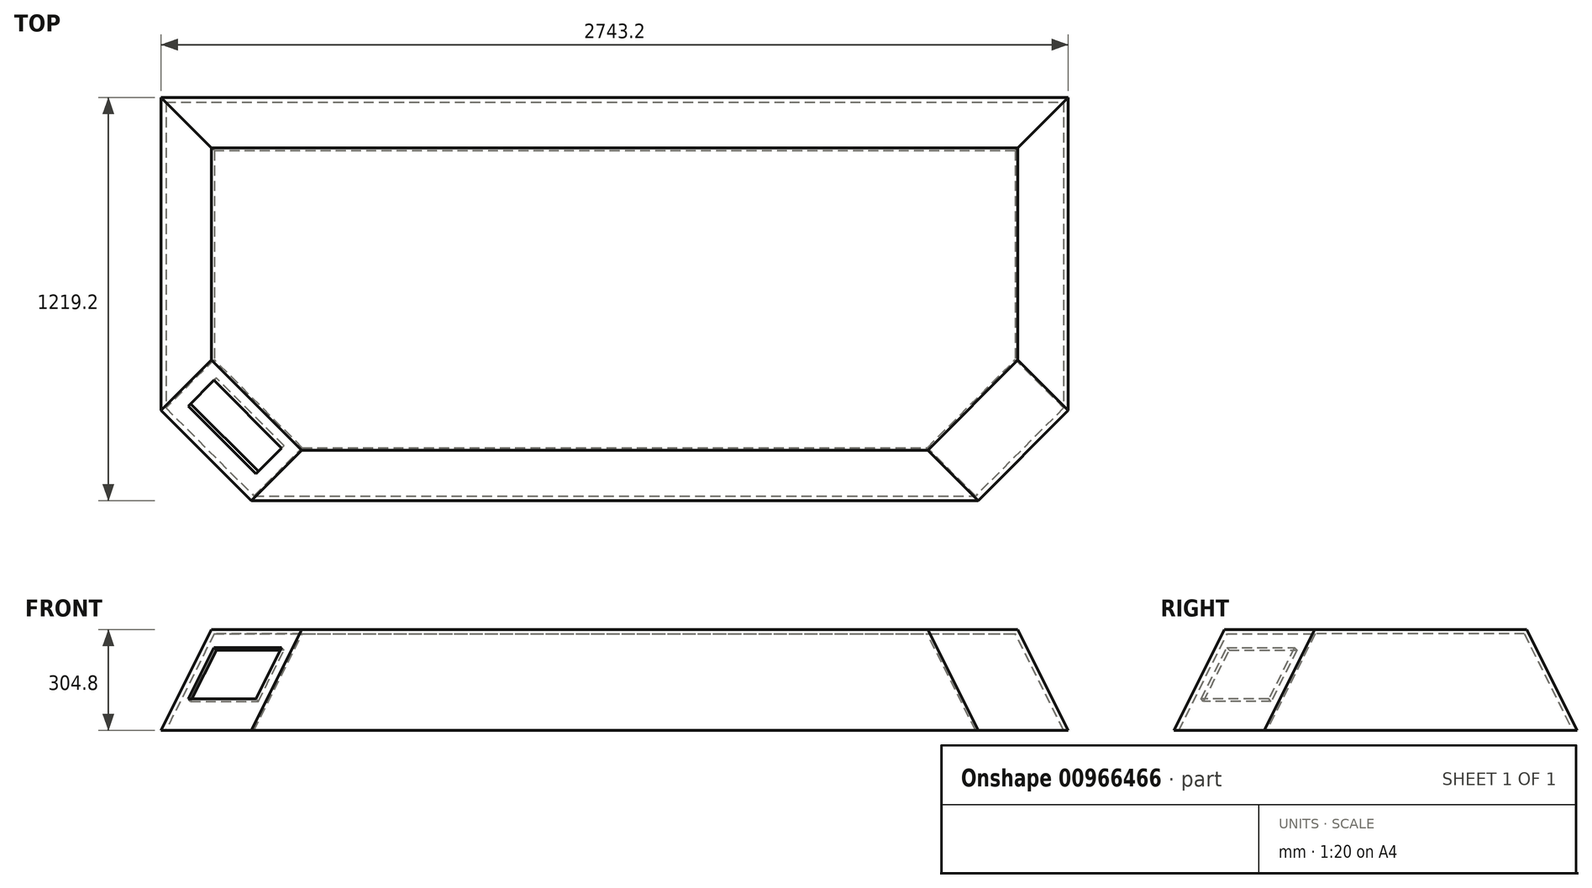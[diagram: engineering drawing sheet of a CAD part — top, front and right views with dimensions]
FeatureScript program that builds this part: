
annotation { "Feature Type Name" : "Feature", "Feature Type Description" : "" }
export const myFeature = defineFeature(function(context is Context, id is Id, definition is map)
    precondition{}
    {
        {
            var Q0;
            Q0=qCreatedBy(makeId("Top.planeOp"),FACE);
            var sketch = newSketch(context, id + "F0", { "sketchPlane" : qUnion([Q0])});
            skLineSegment(sketch, "E0.bottom", {"start": v(-1371.6, 609.6) * mm, "end": v(1371.6, 609.6) * mm});
            skLineSegment(sketch, "E0.top", {"start": v(-1371.6, -609.6) * mm, "end": v(1371.6, -609.6) * mm});
            skLineSegment(sketch, "E0.left", {"start": v(-1371.6, 609.6) * mm, "end": v(-1371.6, -609.6) * mm});
            skLineSegment(sketch, "E0.right", {"start": v(1371.6, 609.6) * mm, "end": v(1371.6, -609.6) * mm});
            skLineSegment(sketch, "E1", {"start": v(-1371.6, 609.6) * mm, "end": v(1371.6, -609.6) * mm, "construction": true});
            skLineSegment(sketch, "E2", {"start": v(-1371.6, -609.6) * mm, "end": v(1371.6, 609.6) * mm, "construction": true});
            skPoint(sketch, "E3", {"position": v(0, 0) * mm});
            skSolve(sketch);
        }
        {
            var Q0;
            Q0=qCreatedBy(makeId("Top.planeOp"),FACE);
            cPlane(context, id + "F1", {"entities" : qUnion([Q0]), "cplaneType" : CPlaneType.OFFSET, "offset" : 304.8 * mm, "width" : 152.4 * mm, "height" : 152.4 * mm});
        }
        {
            var Q0;
            Q0=qCreatedBy(id+"F1.planeOp",FACE);
            var sketch = newSketch(context, id + "F2", { "sketchPlane" : qUnion([Q0])});
            skLineSegment(sketch, "E4.0", {"start": v(-1219.2, 457.2) * mm, "end": v(1219.2, 457.2) * mm});
            skLineSegment(sketch, "E4.1", {"start": v(-1219.2, 457.2) * mm, "end": v(-1219.2, -457.2) * mm});
            skLineSegment(sketch, "E4.2", {"start": v(-1219.2, -457.2) * mm, "end": v(1219.2, -457.2) * mm});
            skLineSegment(sketch, "E4.3", {"start": v(1219.2, 457.2) * mm, "end": v(1219.2, -457.2) * mm});
            skSolve(sketch);
        }
        {
            var Q0;
            Q0=makeQuery(id+"F0.imprint","IMPRINT",FACE,{"disambiguationData":[TD([[makeQuery(id+"F0.imprint","IMPRINT",EDGE,{"derivedFrom":sQuery(id+"F0.wireOp",EDGE,"E0.bottom")}),-1.0]])]});
            var Q1;
            Q1=makeQuery(id+"F2.imprint","IMPRINT",FACE,{"disambiguationData":[TD([[makeQuery(id+"F2.imprint","IMPRINT",EDGE,{"derivedFrom":sQuery(id+"F2.wireOp",EDGE,"E4.0")}),-1.0]])]});
            loft(context, id + "F3", {"sheetProfilesArray" : [{ "sheetProfileEntities" : qUnion([Q0]) }, { "sheetProfileEntities" : qUnion([Q1]) }]});
        }
        {
            var Q0;
            Q0=makeQuery(id+"F3.opLoft","SWEPT_EDGE",EDGE,{"disambiguationData":[OSD([sQuery(id+"F0.wireOp",EDGE,"E0.top"),sQuery(id+"F0.wireOp",EDGE,"E0.right"),sQuery(id+"F2.wireOp",EDGE,"E4.2"),sQuery(id+"F2.wireOp",EDGE,"E4.3")])]});
            var Q1;
            Q1=makeQuery(id+"F3.opLoft","SWEPT_EDGE",EDGE,{"disambiguationData":[OSD([sQuery(id+"F0.wireOp",EDGE,"E0.top"),sQuery(id+"F0.wireOp",EDGE,"E0.left"),sQuery(id+"F2.wireOp",EDGE,"E4.1"),sQuery(id+"F2.wireOp",EDGE,"E4.2")])]});
            chamfer(context, id + "F4", {"entities" : qUnion([Q0, Q1]), "width" : 304.8 * mm, "tangentPropagation" : true});
        }
        {
            var Q0;
            Q0=makeQuery(id+"F3.opLoft","CAP_FACE",FACE,{"disambiguationData":[OSD([makeQuery(id+"F0.imprint","IMPRINT",FACE,{"disambiguationData":[TD([[makeQuery(id+"F0.imprint","IMPRINT",EDGE,{"derivedFrom":sQuery(id+"F0.wireOp",EDGE,"E0.bottom")}),-1.0]])]})])],"isStart":true});
            shell(context, id + "F5", {"entities" : qUnion([Q0]), "thickness" : 12.7 * mm});
        }
        {
            var Q0;
            Q0=makeQuery(id+"F4.opChamfer","BLEND_FACE",FACE,{"disambiguationData":[OSD([sQuery(id+"F0.wireOp",EDGE,"E0.top"),sQuery(id+"F0.wireOp",EDGE,"E0.left"),sQuery(id+"F2.wireOp",EDGE,"E4.1"),sQuery(id+"F2.wireOp",EDGE,"E4.2")])]});
            cPlane(context, id + "F6", {"entities" : qUnion([Q0]), "cplaneType" : CPlaneType.OFFSET, "offset" : 25.4 * mm, "width" : 152.4 * mm, "height" : 152.4 * mm});
        }
        {
            var Q0;
            Q0=qCreatedBy(id+"F6.planeOp",FACE);
            var sketch = newSketch(context, id + "F7", { "sketchPlane" : qUnion([Q0])});
            skLineSegment(sketch, "E5.0", {"start": v(-787.23, 3.42) * mm, "end": v(-536.68, -141.23) * mm});
            skLineSegment(sketch, "E5.1", {"start": v(-882.44, -161.49) * mm, "end": v(-787.23, 3.42) * mm});
            skLineSegment(sketch, "E5.2", {"start": v(-631.89, -306.14) * mm, "end": v(-882.44, -161.49) * mm});
            skLineSegment(sketch, "E5.3", {"start": v(-536.68, -141.23) * mm, "end": v(-631.89, -306.14) * mm});
            skSolve(sketch);
        }
        {
            var Q0;
            Q0=makeQuery(id+"F7.imprint","IMPRINT",FACE,{"disambiguationData":[TD([[makeQuery(id+"F7.imprint","IMPRINT",EDGE,{"derivedFrom":sQuery(id+"F7.wireOp",EDGE,"E5.0")}),-1.0]])]});
            extrude(context, id + "F8", {"entities" : qUnion([Q0]), "operationType" : NewBodyOperationType.REMOVE, "endBound" : BoundingType.THROUGH_ALL, "oppositeDirection" : true, "depth" : 30.48 * mm, "offsetDistance" : 30.48 * mm});
        }
    });
